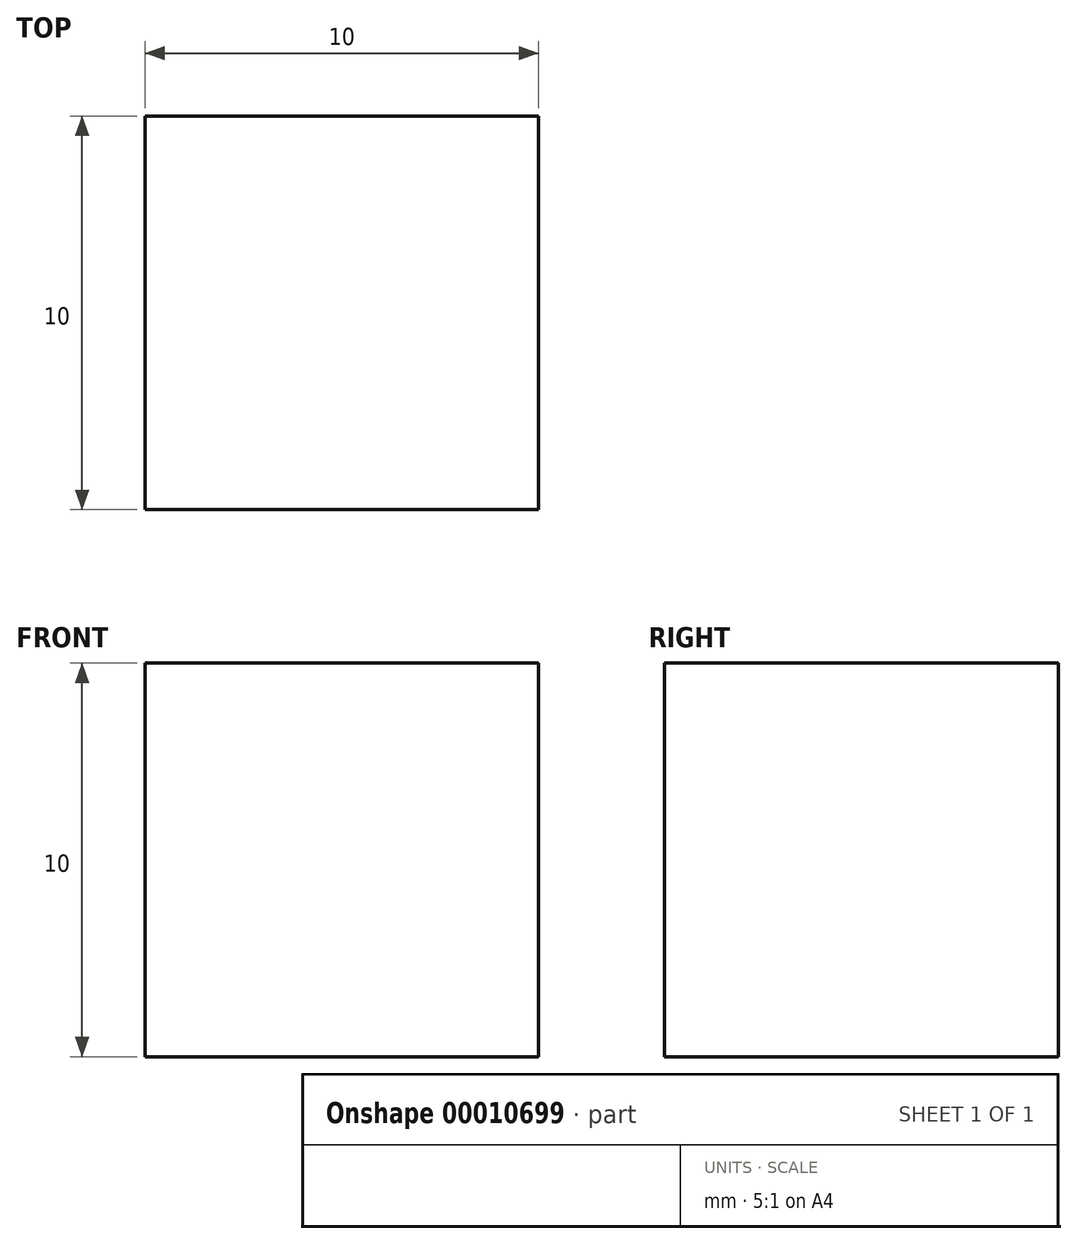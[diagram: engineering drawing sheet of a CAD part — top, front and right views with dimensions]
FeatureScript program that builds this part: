
annotation { "Feature Type Name" : "Feature", "Feature Type Description" : "" }
export const myFeature = defineFeature(function(context is Context, id is Id, definition is map)
    precondition{}
    {
        {
            var Q0;
            Q0=qCreatedBy(makeId("Top.planeOp"),FACE);
            var sketch = newSketch(context, id + "F1", { "sketchPlane" : qUnion([Q0])});
            skLineSegment(sketch, "E0.rect.bottom", {"start": v(5, 5) * mm, "end": v(-5, 5) * mm});
            skLineSegment(sketch, "E0.rect.top", {"start": v(5, -5) * mm, "end": v(-5, -5) * mm});
            skLineSegment(sketch, "E0.rect.left", {"start": v(5, 5) * mm, "end": v(5, -5) * mm});
            skLineSegment(sketch, "E0.rect.right", {"start": v(-5, 5) * mm, "end": v(-5, -5) * mm});
            skPoint(sketch, "E0.rect.middle", {"position": v(0, 0) * mm});
            skPoint(sketch, "E1.rect.left.start.orphan", {"position": v(5.55, 5.55) * mm});
            skPoint(sketch, "E1.rect.top.start.orphan", {"position": v(5.55, -5.55) * mm});
            skPoint(sketch, "E1.rect.right.end.orphan", {"position": v(-5.55, -5.55) * mm});
            skPoint(sketch, "E1.rect.right.start.orphan", {"position": v(-5.55, 5.55) * mm});
            skSolve(sketch);
        }
        {
            var Q0;
            Q0=makeQuery(id+"F1.imprint","IMPRINT",FACE,{"disambiguationData":[TD([[makeQuery(id+"F1.imprint","IMPRINT",EDGE,{"derivedFrom":sQuery(id+"F1.wireOp",EDGE,"E0.rect.bottom")}),-1.0]])]});
            var Q1;
            Q1=makeQuery(id+"F1.imprint","IMPRINT",FACE,{"disambiguationData":[TD([[makeQuery(id+"F1.imprint","IMPRINT",EDGE,{"derivedFrom":sQuery(id+"F1.wireOp",EDGE,"E0.rect.bottom")}),1.0]])]});
            extrude(context, id + "F0", {"entities" : qUnion([Q0, Q1]), "depth" : 10 * mm});
        }
    });
